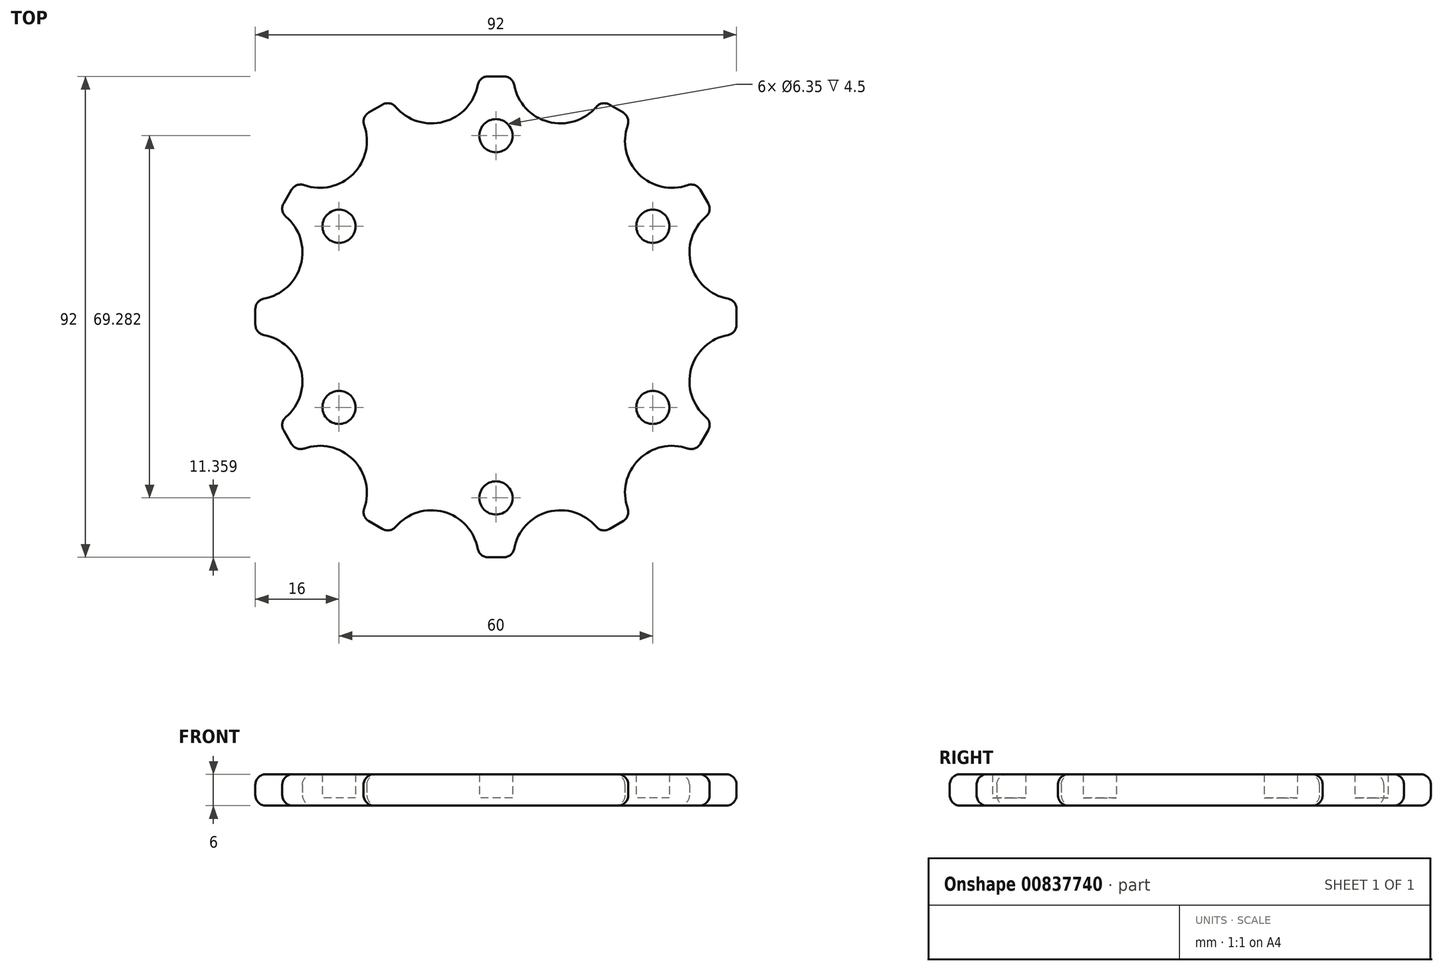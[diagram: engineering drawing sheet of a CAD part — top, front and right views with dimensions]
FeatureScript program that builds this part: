
annotation { "Feature Type Name" : "Feature", "Feature Type Description" : "" }
export const myFeature = defineFeature(function(context is Context, id is Id, definition is map)
    precondition{}
    {
        {
            var Q0;
            Q0=qCreatedBy(makeId("Top.planeOp"),FACE);
            var sketch = newSketch(context, id + "F0", { "sketchPlane" : qUnion([Q0])});
            skCircle(sketch, "E0", {"center": v(0, 0) * mm, "radius": 47.5 * mm});
            skCircle(sketch, "E1.cCircle", {"center": v(0, 0) * mm, "radius": 30 * mm, "construction": true});
            skLineSegment(sketch, "E1.0", {"start": v(30, 17.32) * mm, "end": v(30, -17.32) * mm, "construction": true});
            skLineSegment(sketch, "E1.1", {"start": v(30, -17.32) * mm, "end": v(0, -34.64) * mm, "construction": true});
            skLineSegment(sketch, "E1.2", {"start": v(0, -34.64) * mm, "end": v(-30, -17.32) * mm, "construction": true});
            skLineSegment(sketch, "E1.3", {"start": v(-30, -17.32) * mm, "end": v(-30, 17.32) * mm, "construction": true});
            skLineSegment(sketch, "E1.4", {"start": v(-30, 17.32) * mm, "end": v(0, 34.64) * mm, "construction": true});
            skLineSegment(sketch, "E1.5", {"start": v(0, 34.64) * mm, "end": v(30, 17.32) * mm, "construction": true});
            skPoint(sketch, "E1.0.midPoint", {"position": v(30, 0) * mm});
            skCircle(sketch, "E2", {"center": v(-30, 17.32) * mm, "radius": 3.17 * mm});
            skCircle(sketch, "E3", {"center": v(0, 34.64) * mm, "radius": 3.17 * mm});
            skCircle(sketch, "E4", {"center": v(30, 17.32) * mm, "radius": 3.17 * mm});
            skCircle(sketch, "E5", {"center": v(30, -17.32) * mm, "radius": 3.17 * mm});
            skCircle(sketch, "E6", {"center": v(0, -34.64) * mm, "radius": 3.17 * mm});
            skCircle(sketch, "E7", {"center": v(-30, -17.32) * mm, "radius": 3.17 * mm});
            skSolve(sketch);
        }
        {
            var Q0;
            Q0=makeQuery(id+"F0.imprint","IMPRINT",FACE,{"disambiguationData":[TD([[makeQuery(id+"F0.imprint","IMPRINT",EDGE,{"derivedFrom":sQuery(id+"F0.wireOp",EDGE,"E0")}),1.0]])]});
            var sketch = newSketch(context, id + "F1", { "sketchPlane" : qUnion([Q0])});
            skCircle(sketch, "E8.cCircle", {"center": v(0, 0) * mm, "radius": 46 * mm, "construction": true});
            skLineSegment(sketch, "E8.0", {"start": v(46, 12.33) * mm, "end": v(46, -12.33) * mm});
            skLineSegment(sketch, "E8.1", {"start": v(46, -12.33) * mm, "end": v(33.67, -33.67) * mm});
            skLineSegment(sketch, "E8.2", {"start": v(33.67, -33.67) * mm, "end": v(12.33, -46) * mm});
            skLineSegment(sketch, "E8.3", {"start": v(12.33, -46) * mm, "end": v(-12.33, -46) * mm});
            skLineSegment(sketch, "E8.4", {"start": v(-12.33, -46) * mm, "end": v(-33.67, -33.67) * mm});
            skLineSegment(sketch, "E8.5", {"start": v(-33.67, -33.67) * mm, "end": v(-46, -12.33) * mm});
            skLineSegment(sketch, "E8.6", {"start": v(-46, -12.33) * mm, "end": v(-46, 12.33) * mm});
            skLineSegment(sketch, "E8.7", {"start": v(-46, 12.33) * mm, "end": v(-33.67, 33.67) * mm});
            skLineSegment(sketch, "E8.8", {"start": v(-33.67, 33.67) * mm, "end": v(-12.33, 46) * mm});
            skLineSegment(sketch, "E8.9", {"start": v(-12.33, 46) * mm, "end": v(12.33, 46) * mm});
            skLineSegment(sketch, "E8.10", {"start": v(12.33, 46) * mm, "end": v(33.67, 33.67) * mm});
            skLineSegment(sketch, "E8.11", {"start": v(33.67, 33.67) * mm, "end": v(46, 12.33) * mm});
            skPoint(sketch, "E8.0.midPoint", {"position": v(46, 0) * mm});
            skCircle(sketch, "E9", {"center": v(-46, 12.33) * mm, "radius": 9 * mm});
            skCircle(sketch, "E10", {"center": v(-33.67, 33.67) * mm, "radius": 9 * mm});
            skCircle(sketch, "E11", {"center": v(-12.33, 46) * mm, "radius": 9 * mm});
            skCircle(sketch, "E12", {"center": v(12.33, 46) * mm, "radius": 9 * mm});
            skCircle(sketch, "E13", {"center": v(33.67, 33.67) * mm, "radius": 9 * mm});
            skCircle(sketch, "E14", {"center": v(46, 12.33) * mm, "radius": 9 * mm});
            skCircle(sketch, "E15", {"center": v(46, -12.33) * mm, "radius": 9 * mm});
            skCircle(sketch, "E16", {"center": v(33.67, -33.67) * mm, "radius": 9 * mm});
            skCircle(sketch, "E17", {"center": v(12.33, -46) * mm, "radius": 9 * mm});
            skCircle(sketch, "E18", {"center": v(-12.33, -46) * mm, "radius": 9 * mm});
            skCircle(sketch, "E19", {"center": v(-33.67, -33.67) * mm, "radius": 9 * mm});
            skCircle(sketch, "E20", {"center": v(-46, -12.33) * mm, "radius": 9 * mm});
            skSolve(sketch);
        }
        {
            var Q0;
            {var subQ11=sQuery(id+"F1.wireOp",EDGE,"E8.0");var subQ21=sQuery(id+"F1.wireOp",EDGE,"E14");var subQ34=makeQuery(id+"F1.imprint","INTERSECT",VERTEX,{"derivedFrom":[subQ11,subQ21]});Q0=makeQuery(id+"F1.imprint","IMPRINT",FACE,{"disambiguationData":[TD([[makeQuery(id+"F1.imprint","IMPRINT",EDGE,{"disambiguationData":[TD([[subQ34,-1.0]])],"derivedFrom":subQ11}),-1.0]])]});}
            extrude(context, id + "F2", {"entities" : qUnion([Q0]), "depth" : 6 * mm, "offsetDistance" : 25 * mm});
        }
        {
            var Q0;
            Q0=makeQuery(id+"F0.imprint","IMPRINT",FACE,{"disambiguationData":[TD([[makeQuery(id+"F0.imprint","IMPRINT",EDGE,{"derivedFrom":sQuery(id+"F0.wireOp",EDGE,"E2")}),1.0]])]});
            var Q1;
            Q1=makeQuery(id+"F0.imprint","IMPRINT",FACE,{"disambiguationData":[TD([[makeQuery(id+"F0.imprint","IMPRINT",EDGE,{"derivedFrom":sQuery(id+"F0.wireOp",EDGE,"E3")}),1.0]])]});
            var Q2;
            Q2=makeQuery(id+"F0.imprint","IMPRINT",FACE,{"disambiguationData":[TD([[makeQuery(id+"F0.imprint","IMPRINT",EDGE,{"derivedFrom":sQuery(id+"F0.wireOp",EDGE,"E4")}),1.0]])]});
            var Q3;
            Q3=makeQuery(id+"F0.imprint","IMPRINT",FACE,{"disambiguationData":[TD([[makeQuery(id+"F0.imprint","IMPRINT",EDGE,{"derivedFrom":sQuery(id+"F0.wireOp",EDGE,"E5")}),1.0]])]});
            var Q4;
            Q4=makeQuery(id+"F0.imprint","IMPRINT",FACE,{"disambiguationData":[TD([[makeQuery(id+"F0.imprint","IMPRINT",EDGE,{"derivedFrom":sQuery(id+"F0.wireOp",EDGE,"E6")}),1.0]])]});
            var Q5;
            Q5=makeQuery(id+"F0.imprint","IMPRINT",FACE,{"disambiguationData":[TD([[makeQuery(id+"F0.imprint","IMPRINT",EDGE,{"derivedFrom":sQuery(id+"F0.wireOp",EDGE,"E7")}),1.0]])]});
            extrude(context, id + "F3", {"entities" : qUnion([Q0, Q1, Q2, Q3, Q4, Q5]), "operationType" : NewBodyOperationType.ADD, "depth" : 1.5 * mm, "offsetDistance" : 25 * mm});
        }
        {
            var Q0;
            Q0=makeQuery(id+"F2.opExtrude","CAP_EDGE",EDGE,{"disambiguationData":[OSD([sQuery(id+"F1.wireOp",EDGE,"E20")])],"isStart":true});
            var Q1;
            Q1=makeQuery(id+"F2.opExtrude","SWEPT_FACE",FACE,{"disambiguationData":[OSD([sQuery(id+"F1.wireOp",EDGE,"E8.5")])]});
            var Q2;
            Q2=makeQuery(id+"F2.opExtrude","CAP_EDGE",EDGE,{"disambiguationData":[OSD([sQuery(id+"F1.wireOp",EDGE,"E19")])],"isStart":true});
            var Q3;
            Q3=makeQuery(id+"F2.opExtrude","SWEPT_FACE",FACE,{"disambiguationData":[OSD([sQuery(id+"F1.wireOp",EDGE,"E8.4")])]});
            var Q4;
            Q4=makeQuery(id+"F2.opExtrude","CAP_EDGE",EDGE,{"disambiguationData":[OSD([sQuery(id+"F1.wireOp",EDGE,"E18")])],"isStart":true});
            var Q5;
            Q5=makeQuery(id+"F2.opExtrude","SWEPT_FACE",FACE,{"disambiguationData":[OSD([sQuery(id+"F1.wireOp",EDGE,"E8.3")])]});
            var Q6;
            Q6=makeQuery(id+"F2.opExtrude","CAP_EDGE",EDGE,{"disambiguationData":[OSD([sQuery(id+"F1.wireOp",EDGE,"E17")])],"isStart":true});
            var Q7;
            Q7=makeQuery(id+"F2.opExtrude","SWEPT_FACE",FACE,{"disambiguationData":[OSD([sQuery(id+"F1.wireOp",EDGE,"E8.2")])]});
            var Q8;
            Q8=makeQuery(id+"F2.opExtrude","CAP_EDGE",EDGE,{"disambiguationData":[OSD([sQuery(id+"F1.wireOp",EDGE,"E16")])],"isStart":true});
            var Q9;
            Q9=makeQuery(id+"F2.opExtrude","SWEPT_FACE",FACE,{"disambiguationData":[OSD([sQuery(id+"F1.wireOp",EDGE,"E8.1")])]});
            var Q10;
            Q10=makeQuery(id+"F2.opExtrude","CAP_EDGE",EDGE,{"disambiguationData":[OSD([sQuery(id+"F1.wireOp",EDGE,"E15")])],"isStart":true});
            var Q11;
            Q11=makeQuery(id+"F2.opExtrude","SWEPT_FACE",FACE,{"disambiguationData":[OSD([sQuery(id+"F1.wireOp",EDGE,"E8.0")])]});
            var Q12;
            Q12=makeQuery(id+"F2.opExtrude","CAP_EDGE",EDGE,{"disambiguationData":[OSD([sQuery(id+"F1.wireOp",EDGE,"E14")])],"isStart":true});
            var Q13;
            Q13=makeQuery(id+"F2.opExtrude","SWEPT_FACE",FACE,{"disambiguationData":[OSD([sQuery(id+"F1.wireOp",EDGE,"E8.11")])]});
            var Q14;
            Q14=makeQuery(id+"F2.opExtrude","CAP_EDGE",EDGE,{"disambiguationData":[OSD([sQuery(id+"F1.wireOp",EDGE,"E13")])],"isStart":true});
            var Q15;
            Q15=makeQuery(id+"F2.opExtrude","SWEPT_FACE",FACE,{"disambiguationData":[OSD([sQuery(id+"F1.wireOp",EDGE,"E8.10")])]});
            var Q16;
            Q16=makeQuery(id+"F2.opExtrude","CAP_EDGE",EDGE,{"disambiguationData":[OSD([sQuery(id+"F1.wireOp",EDGE,"E12")])],"isStart":true});
            var Q17;
            Q17=makeQuery(id+"F2.opExtrude","SWEPT_FACE",FACE,{"disambiguationData":[OSD([sQuery(id+"F1.wireOp",EDGE,"E8.9")])]});
            var Q18;
            Q18=makeQuery(id+"F2.opExtrude","CAP_EDGE",EDGE,{"disambiguationData":[OSD([sQuery(id+"F1.wireOp",EDGE,"E11")])],"isStart":true});
            var Q19;
            Q19=makeQuery(id+"F2.opExtrude","SWEPT_FACE",FACE,{"disambiguationData":[OSD([sQuery(id+"F1.wireOp",EDGE,"E8.8")])]});
            var Q20;
            Q20=makeQuery(id+"F2.opExtrude","CAP_EDGE",EDGE,{"disambiguationData":[OSD([sQuery(id+"F1.wireOp",EDGE,"E10")])],"isStart":true});
            var Q21;
            Q21=makeQuery(id+"F2.opExtrude","SWEPT_FACE",FACE,{"disambiguationData":[OSD([sQuery(id+"F1.wireOp",EDGE,"E8.7")])]});
            var Q22;
            Q22=makeQuery(id+"F2.opExtrude","CAP_EDGE",EDGE,{"disambiguationData":[OSD([sQuery(id+"F1.wireOp",EDGE,"E9")])],"isStart":true});
            var Q23;
            Q23=makeQuery(id+"F2.opExtrude","SWEPT_FACE",FACE,{"disambiguationData":[OSD([sQuery(id+"F1.wireOp",EDGE,"E8.6")])]});
            fillet(context, id + "F4", {"entities" : qUnion([Q0, Q1, Q2, Q3, Q4, Q5, Q6, Q7, Q8, Q9, Q10, Q11, Q12, Q13, Q14, Q15, Q16, Q17, Q18, Q19, Q20, Q21, Q22, Q23]), "radius" : 2 * mm, "tangentPropagation" : true, "allowEdgeOverflow" : false});
        }
        {
            var Q0;
            Q0=makeQuery(id+"F2.opExtrude","CAP_EDGE",EDGE,{"disambiguationData":[OSD([sQuery(id+"F1.wireOp",EDGE,"E17")])],"isStart":false});
            var Q1;
            Q1=makeQuery(id+"F2.opExtrude","CAP_EDGE",EDGE,{"disambiguationData":[OSD([sQuery(id+"F1.wireOp",EDGE,"E16")])],"isStart":false});
            var Q2;
            Q2=makeQuery(id+"F2.opExtrude","CAP_EDGE",EDGE,{"disambiguationData":[OSD([sQuery(id+"F1.wireOp",EDGE,"E15")])],"isStart":false});
            var Q3;
            Q3=makeQuery(id+"F2.opExtrude","CAP_EDGE",EDGE,{"disambiguationData":[OSD([sQuery(id+"F1.wireOp",EDGE,"E14")])],"isStart":false});
            var Q4;
            Q4=makeQuery(id+"F2.opExtrude","CAP_EDGE",EDGE,{"disambiguationData":[OSD([sQuery(id+"F1.wireOp",EDGE,"E13")])],"isStart":false});
            var Q5;
            Q5=makeQuery(id+"F2.opExtrude","CAP_EDGE",EDGE,{"disambiguationData":[OSD([sQuery(id+"F1.wireOp",EDGE,"E12")])],"isStart":false});
            var Q6;
            Q6=makeQuery(id+"F2.opExtrude","CAP_EDGE",EDGE,{"disambiguationData":[OSD([sQuery(id+"F1.wireOp",EDGE,"E11")])],"isStart":false});
            var Q7;
            Q7=makeQuery(id+"F2.opExtrude","CAP_EDGE",EDGE,{"disambiguationData":[OSD([sQuery(id+"F1.wireOp",EDGE,"E10")])],"isStart":false});
            var Q8;
            Q8=makeQuery(id+"F2.opExtrude","CAP_EDGE",EDGE,{"disambiguationData":[OSD([sQuery(id+"F1.wireOp",EDGE,"E9")])],"isStart":false});
            var Q9;
            Q9=makeQuery(id+"F2.opExtrude","CAP_EDGE",EDGE,{"disambiguationData":[OSD([sQuery(id+"F1.wireOp",EDGE,"E20")])],"isStart":false});
            var Q10;
            Q10=makeQuery(id+"F2.opExtrude","CAP_EDGE",EDGE,{"disambiguationData":[OSD([sQuery(id+"F1.wireOp",EDGE,"E19")])],"isStart":false});
            var Q11;
            Q11=makeQuery(id+"F2.opExtrude","CAP_EDGE",EDGE,{"disambiguationData":[OSD([sQuery(id+"F1.wireOp",EDGE,"E18")])],"isStart":false});
            fillet(context, id + "F5", {"entities" : qUnion([Q0, Q1, Q2, Q3, Q4, Q5, Q6, Q7, Q8, Q9, Q10, Q11]), "radius" : 2 * mm, "tangentPropagation" : true, "allowEdgeOverflow" : false});
        }
    });
